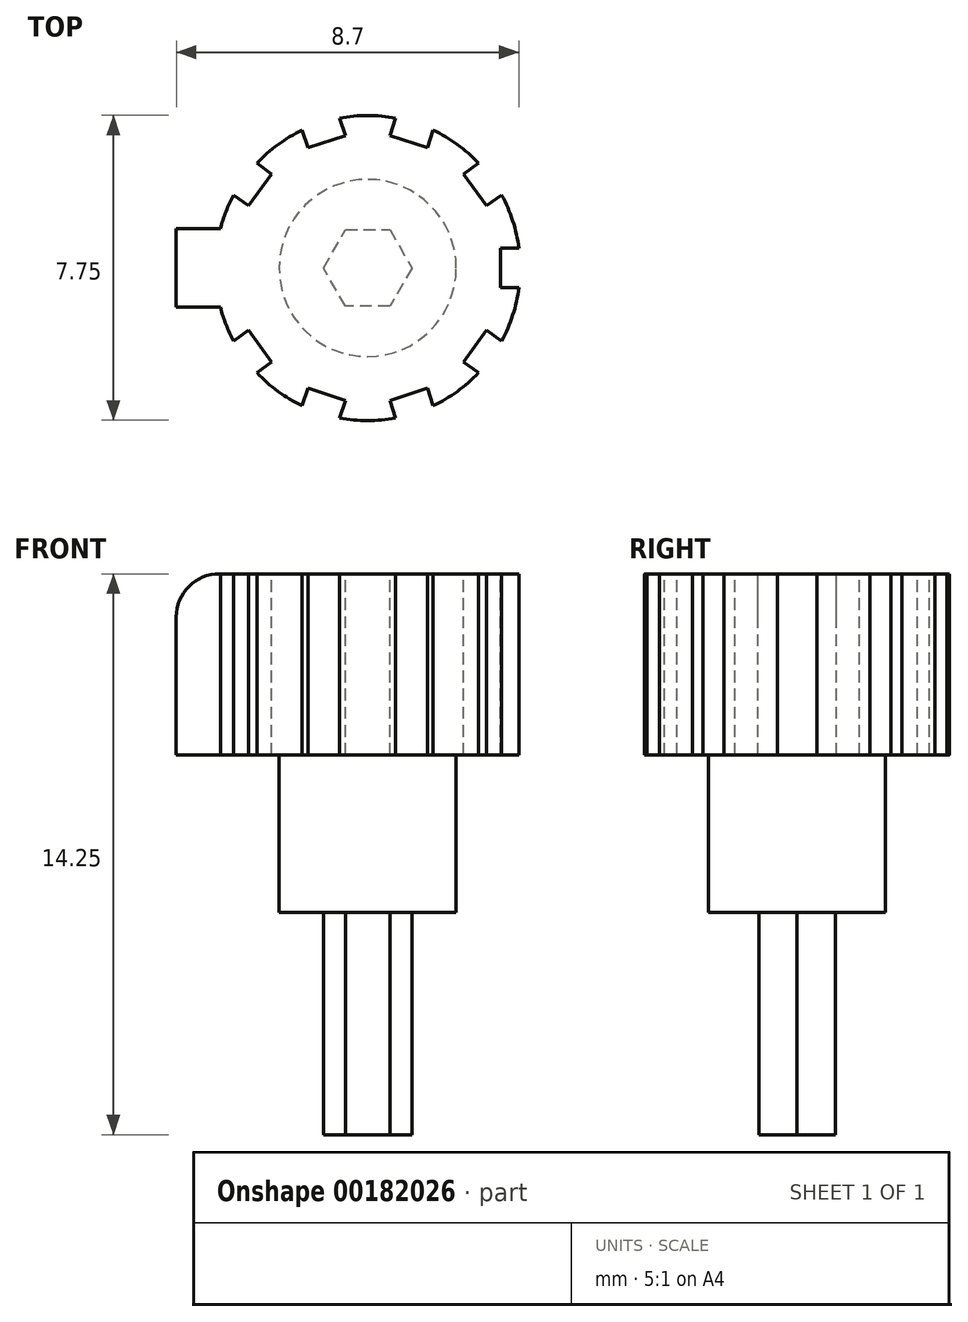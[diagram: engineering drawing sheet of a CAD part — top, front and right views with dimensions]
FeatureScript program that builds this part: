
annotation { "Feature Type Name" : "Feature", "Feature Type Description" : "" }
export const myFeature = defineFeature(function(context is Context, id is Id, definition is map)
    precondition{}
    {
        {
            var Q0;
            Q0=qCreatedBy(makeId("Top.planeOp"),FACE);
            var sketch = newSketch(context, id + "F0", { "sketchPlane" : qUnion([Q0])});
            skCircle(sketch, "E0.cCircle", {"center": v(0, 0) * mm, "radius": 1.13 * mm, "construction": true});
            skLineSegment(sketch, "E0.0", {"start": v(0.56, -0.97) * mm, "end": v(-0.56, -0.97) * mm});
            skLineSegment(sketch, "E0.1", {"start": v(-0.56, -0.97) * mm, "end": v(-1.13, 0) * mm});
            skLineSegment(sketch, "E0.2", {"start": v(-1.13, 0) * mm, "end": v(-0.56, 0.97) * mm});
            skLineSegment(sketch, "E0.3", {"start": v(-0.56, 0.97) * mm, "end": v(0.56, 0.97) * mm});
            skLineSegment(sketch, "E0.4", {"start": v(0.56, 0.97) * mm, "end": v(1.13, 0) * mm});
            skLineSegment(sketch, "E0.5", {"start": v(1.13, 0) * mm, "end": v(0.56, -0.97) * mm});
            skLineSegment(sketch, "E1", {"start": v(0, 2.12) * mm, "end": v(0, -2.1) * mm, "construction": true});
            skSolve(sketch);
        }
        {
            var Q0;
            Q0 = qSketchRegion(id + "F0", true);
            extrude(context, id + "F1", {"entities" : qUnion([Q0]), "depth" : 5.65 * mm});
        }
        {
            var Q0;
            Q0=makeQuery(id+"F1.opExtrude","CAP_FACE",FACE,{"disambiguationData":[OSD([sQuery(id+"F0.wireOp",EDGE,"E0.0"),sQuery(id+"F0.wireOp",EDGE,"E0.1"),sQuery(id+"F0.wireOp",EDGE,"E0.2"),sQuery(id+"F0.wireOp",EDGE,"E0.3"),sQuery(id+"F0.wireOp",EDGE,"E0.4"),sQuery(id+"F0.wireOp",EDGE,"E0.5")])],"isStart":false});
            var sketch = newSketch(context, id + "F2", { "sketchPlane" : qUnion([Q0])});
            skCircle(sketch, "E2", {"center": v(0, 0) * mm, "radius": 2.25 * mm});
            skSolve(sketch);
        }
        {
            var Q0;
            Q0 = qSketchRegion(id + "F2", true);
            extrude(context, id + "F3", {"entities" : qUnion([Q0]), "operationType" : NewBodyOperationType.ADD, "depth" : 4 * mm});
        }
        {
            var Q0;
            Q0=makeQuery(id+"F3.opExtrude","CAP_FACE",FACE,{"disambiguationData":[OSD([sQuery(id+"F2.wireOp",EDGE,"E2")])],"isStart":false});
            var sketch = newSketch(context, id + "F4", { "sketchPlane" : qUnion([Q0])});
            skCircle(sketch, "E3", {"center": v(0, 0) * mm, "radius": 3.88 * mm});
            skSolve(sketch);
        }
        {
            var Q0;
            Q0 = qSketchRegion(id + "F4", true);
            extrude(context, id + "F5", {"entities" : qUnion([Q0]), "operationType" : NewBodyOperationType.ADD, "depth" : 4.6 * mm});
        }
        {
            var Q0;
            Q0=makeQuery(id+"F5.opExtrude","CAP_FACE",FACE,{"disambiguationData":[OSD([sQuery(id+"F4.wireOp",EDGE,"E3")])],"isStart":false});
            var sketch = newSketch(context, id + "F6", { "sketchPlane" : qUnion([Q0])});
            skLineSegment(sketch, "E4.bottom", {"start": v(4.38, -0.5) * mm, "end": v(3.38, -0.5) * mm});
            skLineSegment(sketch, "E4.top", {"start": v(4.38, 0.5) * mm, "end": v(3.38, 0.5) * mm});
            skLineSegment(sketch, "E4.left", {"start": v(4.38, -0.5) * mm, "end": v(4.38, 0.5) * mm});
            skLineSegment(sketch, "E4.right", {"start": v(3.38, -0.5) * mm, "end": v(3.38, 0.5) * mm});
            skPoint(sketch, "E4.middle", {"position": v(3.88, 0) * mm});
            skSolve(sketch);
        }
        {
            var Q0;
            {var subQ0=sQuery(id+"F6.wireOp",EDGE,"E4.left");Q0=makeQuery(id+"F6.imprint","IMPRINT",FACE,{"disambiguationData":[TD([[makeQuery(id+"F6.imprint","IMPRINT",EDGE,{"derivedFrom":subQ0}),1.0]])]});}
            var Q1;
            {var subQ0=sQuery(id+"F6.wireOp",EDGE,"E4.right");Q1=makeQuery(id+"F6.imprint","IMPRINT",FACE,{"disambiguationData":[TD([[makeQuery(id+"F6.imprint","IMPRINT",EDGE,{"derivedFrom":subQ0}),-1.0]])]});}
            extrude(context, id + "F7", {"entities" : qUnion([Q0, Q1]), "oppositeDirection" : true, "depth" : 5 * mm});
        }
        {
            var Q0;
            Q0=qCreatedBy(makeId("Front.planeOp"),FACE);
            var sketch = newSketch(context, id + "F8", { "sketchPlane" : qUnion([Q0])});
            skLineSegment(sketch, "E5", {"start": v(0, 17.26) * mm, "end": v(0, -2.53) * mm, "construction": true});
            skSolve(sketch);
        }
        {
            var Q0;
            Q0=makeQuery(id+"F7.opExtrude","SWEPT_BODY",BODY,{"disambiguationData":[OSD([sQuery(id+"F6.wireOp",EDGE,"E4.bottom"),sQuery(id+"F6.wireOp",EDGE,"E4.top"),sQuery(id+"F6.wireOp",EDGE,"E4.left"),sQuery(id+"F6.wireOp",EDGE,"E4.right")])]});
            var Q1;
            Q1=sQuery(id+"F8.wireOp",EDGE,"E5");
            circularPattern(context, id + "F9", {"entities" : qUnion([Q0]), "axis" : qUnion([Q1]), "angle" : 360 * degree, "instanceCount" : 10, "equalSpace" : true});
        }
        {
            var Q0;
            Q0=makeQuery(id+"F7.opExtrude","SWEPT_BODY",BODY,{"disambiguationData":[OSD([sQuery(id+"F6.wireOp",EDGE,"E4.bottom"),sQuery(id+"F6.wireOp",EDGE,"E4.top"),sQuery(id+"F6.wireOp",EDGE,"E4.left"),sQuery(id+"F6.wireOp",EDGE,"E4.right")])]});
            var Q1;
            Q1=makeQuery(id+"F9.opPattern","COPY",BODY,{"derivedFrom":makeQuery(id+"F7.opExtrude","SWEPT_BODY",BODY,{"disambiguationData":[OSD([sQuery(id+"F6.wireOp",EDGE,"E4.bottom"),sQuery(id+"F6.wireOp",EDGE,"E4.top"),sQuery(id+"F6.wireOp",EDGE,"E4.left"),sQuery(id+"F6.wireOp",EDGE,"E4.right")])]}),"instanceName":"1"});
            var Q2;
            Q2=makeQuery(id+"F9.opPattern","COPY",BODY,{"derivedFrom":makeQuery(id+"F7.opExtrude","SWEPT_BODY",BODY,{"disambiguationData":[OSD([sQuery(id+"F6.wireOp",EDGE,"E4.bottom"),sQuery(id+"F6.wireOp",EDGE,"E4.top"),sQuery(id+"F6.wireOp",EDGE,"E4.left"),sQuery(id+"F6.wireOp",EDGE,"E4.right")])]}),"instanceName":"2"});
            var Q3;
            Q3=makeQuery(id+"F9.opPattern","COPY",BODY,{"derivedFrom":makeQuery(id+"F7.opExtrude","SWEPT_BODY",BODY,{"disambiguationData":[OSD([sQuery(id+"F6.wireOp",EDGE,"E4.bottom"),sQuery(id+"F6.wireOp",EDGE,"E4.top"),sQuery(id+"F6.wireOp",EDGE,"E4.left"),sQuery(id+"F6.wireOp",EDGE,"E4.right")])]}),"instanceName":"3"});
            var Q4;
            Q4=makeQuery(id+"F9.opPattern","COPY",BODY,{"derivedFrom":makeQuery(id+"F7.opExtrude","SWEPT_BODY",BODY,{"disambiguationData":[OSD([sQuery(id+"F6.wireOp",EDGE,"E4.bottom"),sQuery(id+"F6.wireOp",EDGE,"E4.top"),sQuery(id+"F6.wireOp",EDGE,"E4.left"),sQuery(id+"F6.wireOp",EDGE,"E4.right")])]}),"instanceName":"4"});
            var Q5;
            Q5=makeQuery(id+"F9.opPattern","COPY",BODY,{"derivedFrom":makeQuery(id+"F7.opExtrude","SWEPT_BODY",BODY,{"disambiguationData":[OSD([sQuery(id+"F6.wireOp",EDGE,"E4.bottom"),sQuery(id+"F6.wireOp",EDGE,"E4.top"),sQuery(id+"F6.wireOp",EDGE,"E4.left"),sQuery(id+"F6.wireOp",EDGE,"E4.right")])]}),"instanceName":"5"});
            var Q6;
            Q6=makeQuery(id+"F9.opPattern","COPY",BODY,{"derivedFrom":makeQuery(id+"F7.opExtrude","SWEPT_BODY",BODY,{"disambiguationData":[OSD([sQuery(id+"F6.wireOp",EDGE,"E4.bottom"),sQuery(id+"F6.wireOp",EDGE,"E4.top"),sQuery(id+"F6.wireOp",EDGE,"E4.left"),sQuery(id+"F6.wireOp",EDGE,"E4.right")])]}),"instanceName":"6"});
            var Q7;
            Q7=makeQuery(id+"F9.opPattern","COPY",BODY,{"derivedFrom":makeQuery(id+"F7.opExtrude","SWEPT_BODY",BODY,{"disambiguationData":[OSD([sQuery(id+"F6.wireOp",EDGE,"E4.bottom"),sQuery(id+"F6.wireOp",EDGE,"E4.top"),sQuery(id+"F6.wireOp",EDGE,"E4.left"),sQuery(id+"F6.wireOp",EDGE,"E4.right")])]}),"instanceName":"7"});
            var Q8;
            Q8=makeQuery(id+"F9.opPattern","COPY",BODY,{"derivedFrom":makeQuery(id+"F7.opExtrude","SWEPT_BODY",BODY,{"disambiguationData":[OSD([sQuery(id+"F6.wireOp",EDGE,"E4.bottom"),sQuery(id+"F6.wireOp",EDGE,"E4.top"),sQuery(id+"F6.wireOp",EDGE,"E4.left"),sQuery(id+"F6.wireOp",EDGE,"E4.right")])]}),"instanceName":"8"});
            var Q9;
            Q9=makeQuery(id+"F9.opPattern","COPY",BODY,{"derivedFrom":makeQuery(id+"F7.opExtrude","SWEPT_BODY",BODY,{"disambiguationData":[OSD([sQuery(id+"F6.wireOp",EDGE,"E4.bottom"),sQuery(id+"F6.wireOp",EDGE,"E4.top"),sQuery(id+"F6.wireOp",EDGE,"E4.left"),sQuery(id+"F6.wireOp",EDGE,"E4.right")])]}),"instanceName":"9"});
            var Q10;
            Q10=makeQuery(id+"F1.opExtrude","SWEPT_BODY",BODY,{"disambiguationData":[OSD([sQuery(id+"F0.wireOp",EDGE,"E0.0"),sQuery(id+"F0.wireOp",EDGE,"E0.1"),sQuery(id+"F0.wireOp",EDGE,"E0.2"),sQuery(id+"F0.wireOp",EDGE,"E0.3"),sQuery(id+"F0.wireOp",EDGE,"E0.4"),sQuery(id+"F0.wireOp",EDGE,"E0.5")])]});
            booleanBodies(context, id + "F10", {"operationType" : BooleanOperationType.SUBTRACTION, "tools" : qUnion([Q0, Q1, Q2, Q3, Q4, Q5, Q6, Q7, Q8, Q9]), "targets" : qUnion([Q10])});
        }
        {
            var Q0;
            Q0=makeQuery(id+"F5.opExtrude","CAP_FACE",FACE,{"disambiguationData":[OSD([sQuery(id+"F4.wireOp",EDGE,"E3")])],"isStart":false});
            var sketch = newSketch(context, id + "F11", { "sketchPlane" : qUnion([Q0])});
            skLineSegment(sketch, "E6.bottom", {"start": v(1.57, -1) * mm, "end": v(-4.86, -1) * mm});
            skLineSegment(sketch, "E6.top", {"start": v(1.57, 1) * mm, "end": v(-4.86, 1) * mm});
            skLineSegment(sketch, "E6.left", {"start": v(1.57, -1) * mm, "end": v(1.57, 1) * mm});
            skLineSegment(sketch, "E6.right", {"start": v(-4.86, -1) * mm, "end": v(-4.86, 1) * mm});
            skPoint(sketch, "E6.middle", {"position": v(-1.65, 0) * mm});
            skSolve(sketch);
        }
        {
            var Q0;
            {var subQ2=sQuery(id+"F11.wireOp",EDGE,"E6.right");Q0=makeQuery(id+"F11.imprint","IMPRINT",FACE,{"disambiguationData":[TD([[makeQuery(id+"F11.imprint","IMPRINT",EDGE,{"derivedFrom":subQ2}),-1.0]])]});}
            extrude(context, id + "F12", {"entities" : qUnion([Q0]), "operationType" : NewBodyOperationType.ADD, "oppositeDirection" : true, "depth" : 4.6 * mm});
        }
        {
            var Q0;
            Q0=makeQuery(id+"F12.opExtrude","CAP_EDGE",EDGE,{"disambiguationData":[OSD([sQuery(id+"F11.wireOp",EDGE,"E6.right")])],"isStart":true});
            fillet(context, id + "F13", {"entities" : qUnion([Q0]), "radius" : 1.1 * mm, "tangentPropagation" : true, "allowEdgeOverflow" : false});
        }
    });
